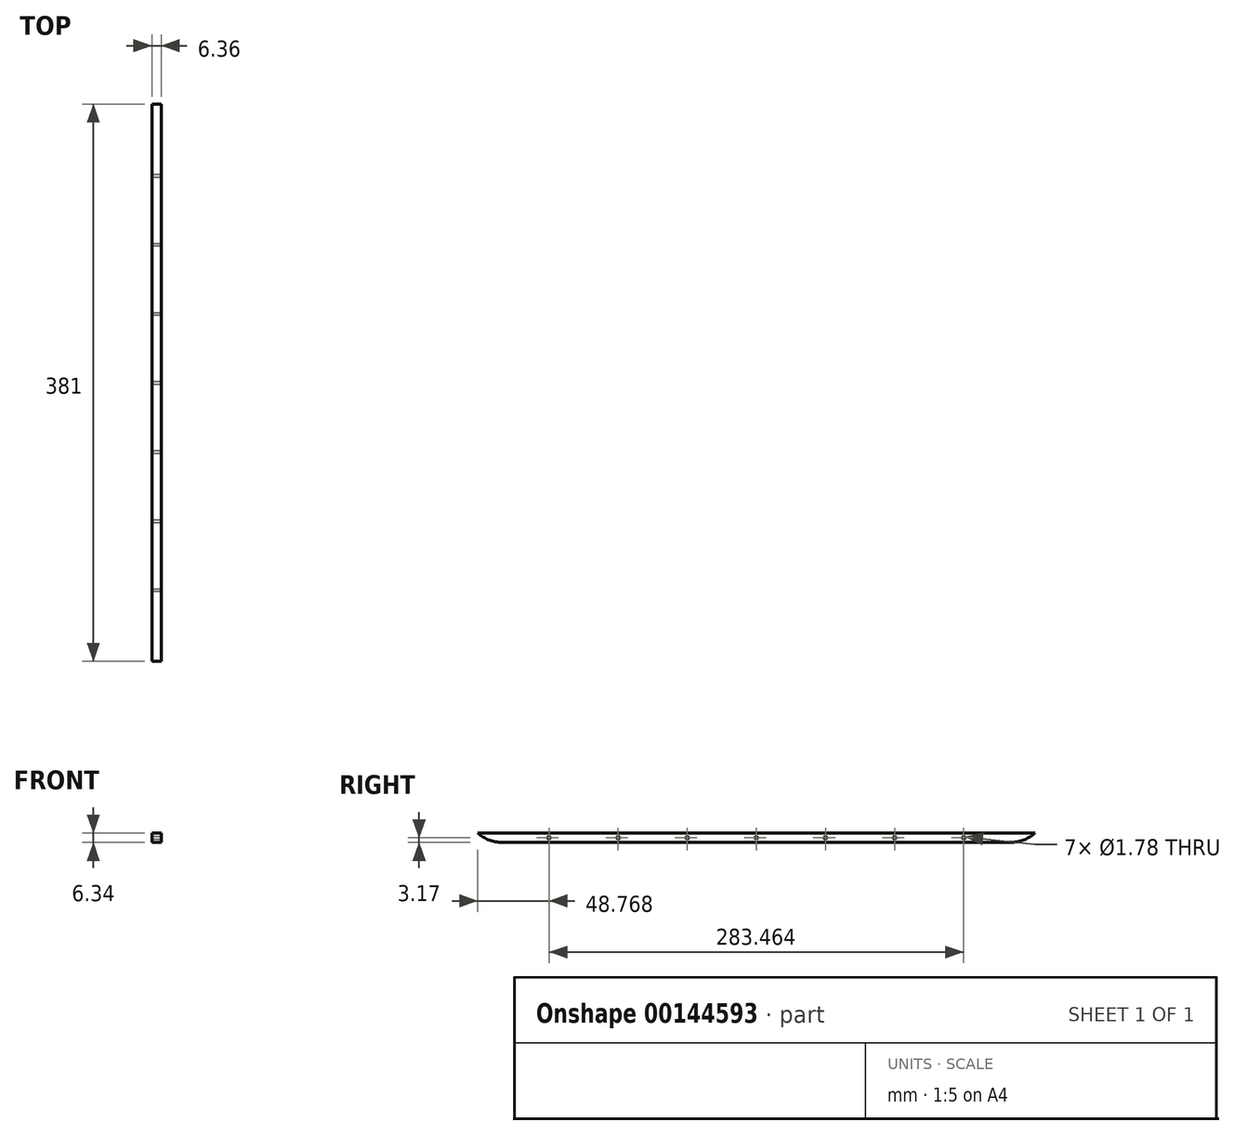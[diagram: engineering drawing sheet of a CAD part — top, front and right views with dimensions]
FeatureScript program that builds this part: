
annotation { "Feature Type Name" : "Feature", "Feature Type Description" : "" }
export const myFeature = defineFeature(function(context is Context, id is Id, definition is map)
    precondition{}
    {
        {
            var Q0;
            Q0=qCreatedBy(makeId("Front.planeOp"),FACE);
            var sketch = newSketch(context, id + "F0", { "sketchPlane" : qUnion([Q0])});
            skLineSegment(sketch, "E0.bottom", {"start": v(3.18, -3.18) * mm, "end": v(-3.17, -3.18) * mm});
            skLineSegment(sketch, "E0.top", {"start": v(3.18, 3.18) * mm, "end": v(-3.18, 3.18) * mm});
            skLineSegment(sketch, "E0.left", {"start": v(3.18, -3.18) * mm, "end": v(3.18, 3.18) * mm});
            skLineSegment(sketch, "E0.right", {"start": v(-3.18, -3.18) * mm, "end": v(-3.18, 3.17) * mm});
            skPoint(sketch, "E0.middle", {"position": v(0, 0) * mm});
            skSolve(sketch);
        }
        {
            var Q0;
            Q0=makeQuery(id+"F0.imprint","IMPRINT",FACE,{"disambiguationData":[TD([[makeQuery(id+"F0.imprint","IMPRINT",EDGE,{"derivedFrom":sQuery(id+"F0.wireOp",EDGE,"E0.bottom")}),-1.0]])]});
            extrude(context, id + "F1", {"entities" : qUnion([Q0]), "endBound" : BoundingType.SYMMETRIC, "depth" : 381 * mm});
        }
        {
            var Q0;
            Q0=makeQuery(id+"F1.opExtrude","CAP_EDGE",EDGE,{"disambiguationData":[OSD([sQuery(id+"F0.wireOp",EDGE,"E0.bottom")])],"isStart":false});
            var Q1;
            Q1=makeQuery(id+"F1.opExtrude","CAP_EDGE",EDGE,{"disambiguationData":[OSD([sQuery(id+"F0.wireOp",EDGE,"E0.bottom")])],"isStart":true});
            fillet(context, id + "F2", {"entities" : qUnion([Q0, Q1]), "radius" : 25.4 * mm, "tangentPropagation" : true, "allowEdgeOverflow" : false});
        }
        {
            var Q0;
            Q0=makeQuery(id+"F1.opExtrude","SWEPT_FACE",FACE,{"disambiguationData":[OSD([sQuery(id+"F0.wireOp",EDGE,"E0.left")])]});
            var sketch = newSketch(context, id + "F3", { "sketchPlane" : qUnion([Q0])});
            skPoint(sketch, "E1", {"position": v(0, 0) * mm});
            skPoint(sketch, "E2.1.0.0", {"position": v(47.24, 0) * mm});
            skPoint(sketch, "E2.2.0.0", {"position": v(94.49, 0) * mm});
            skPoint(sketch, "E2.3.0.0", {"position": v(141.73, 0) * mm});
            skLineSegment(sketch, "E2.direction1", {"start": v(0, 0) * mm, "end": v(47.24, 0) * mm, "construction": true});
            skPoint(sketch, "E3.MirrorP", {"position": v(-47.24, 0) * mm});
            skPoint(sketch, "E4.MirrorP", {"position": v(-94.49, 0) * mm});
            skPoint(sketch, "E5.MirrorP", {"position": v(-141.73, 0) * mm});
            skSolve(sketch);
        }
        {
            var Q0;
            Q0=sQuery(id+"F3.wireOp",VERTEX,"E2.1.0.0");
            var Q1;
            Q1=sQuery(id+"F3.wireOp",VERTEX,"E2.2.0.0");
            var Q2;
            Q2=sQuery(id+"F3.wireOp",VERTEX,"E2.3.0.0");
            var Q3;
            Q3=sQuery(id+"F3.wireOp",VERTEX,"E1");
            var Q4;
            Q4=sQuery(id+"F3.wireOp",VERTEX,"E3.MirrorP");
            var Q5;
            Q5=sQuery(id+"F3.wireOp",VERTEX,"E4.MirrorP");
            var Q6;
            Q6=sQuery(id+"F3.wireOp",VERTEX,"E5.MirrorP");
            var Q7;
            Q7=makeQuery(id+"F1.opExtrude","SWEPT_BODY",BODY,{"disambiguationData":[OSD([sQuery(id+"F0.wireOp",EDGE,"E0.bottom"),sQuery(id+"F0.wireOp",EDGE,"E0.top"),sQuery(id+"F0.wireOp",EDGE,"E0.left"),sQuery(id+"F0.wireOp",EDGE,"E0.right")])]});
            hole(context, id + "F4", {"style" : HoleStyle.SIMPLE, "endStyle" : HoleEndStyle.THROUGH, "standardTappedOrClearance" : lookupTablePath({ "standard" : "ANSI", "fit" : "Normal (ASME)", "size" : "#0", "type" : "Clearance" }), "standardBlindInLast" : lookupTablePath({ "fit" : "Free", "standard" : "ANSI", "size" : "#0", "type" : "Clearance" }), "holeDiameter" : 1.78 * mm, "startFromSketch" : true, "locations" : qUnion([Q0, Q1, Q2, Q3, Q4, Q5, Q6]), "scope" : qUnion([Q7]), "isTappedThrough" : true});
        }
    });
